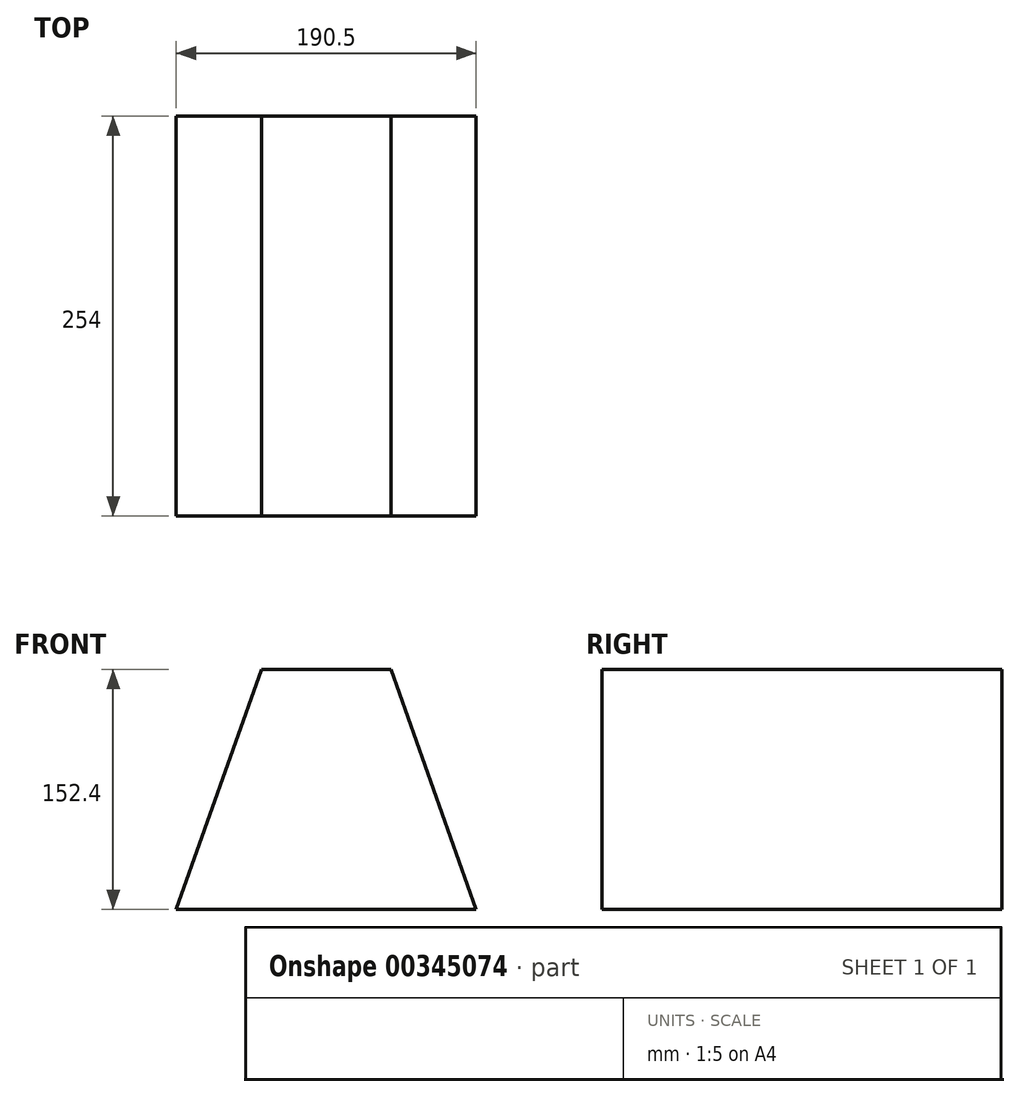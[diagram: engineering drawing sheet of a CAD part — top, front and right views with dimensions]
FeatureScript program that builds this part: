
annotation { "Feature Type Name" : "Feature", "Feature Type Description" : "" }
export const myFeature = defineFeature(function(context is Context, id is Id, definition is map)
    precondition{}
    {
        {
            var Q0;
            Q0=qCreatedBy(makeId("Front.planeOp"),FACE);
            var sketch = newSketch(context, id + "F0", { "sketchPlane" : qUnion([Q0])});
            skLineSegment(sketch, "E0", {"start": v(-41.04, 76.2) * mm, "end": v(41.04, 76.2) * mm});
            skLineSegment(sketch, "E1", {"start": v(41.04, 76.2) * mm, "end": v(95.25, -76.2) * mm});
            skLineSegment(sketch, "E2", {"start": v(95.25, -76.2) * mm, "end": v(-95.25, -76.2) * mm});
            skLineSegment(sketch, "E3", {"start": v(-95.25, -76.2) * mm, "end": v(-41.04, 76.2) * mm});
            skSolve(sketch);
        }
        {
            var Q0;
            Q0 = qSketchRegion(id + "F0", true);
            extrude(context, id + "F1", {"entities" : qUnion([Q0]), "depth" : 254 * mm});
        }
    });
